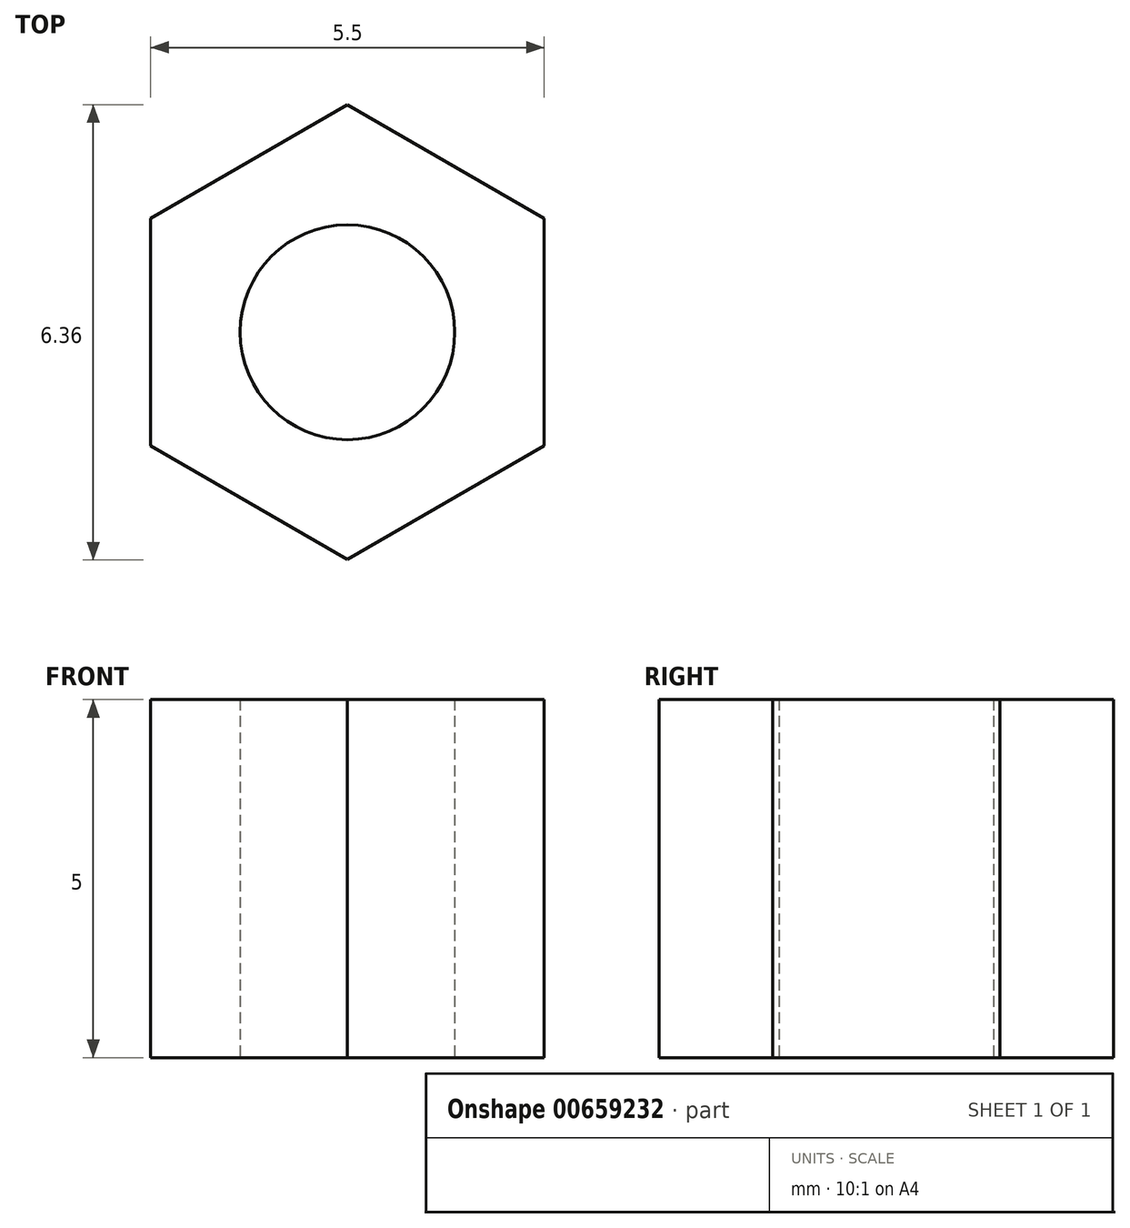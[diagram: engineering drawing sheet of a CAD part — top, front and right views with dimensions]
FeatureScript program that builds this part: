
annotation { "Feature Type Name" : "Feature", "Feature Type Description" : "" }
export const myFeature = defineFeature(function(context is Context, id is Id, definition is map)
    precondition{}
    {
        {
            var Q0;
            Q0=qCreatedBy(makeId("Top.planeOp"),FACE);
            var sketch = newSketch(context, id + "F0", { "sketchPlane" : qUnion([Q0])});
            skCircle(sketch, "E0.cCircle", {"center": v(0, 0) * mm, "radius": 2.75 * mm, "construction": true});
            skLineSegment(sketch, "E0.0", {"start": v(2.75, 1.59) * mm, "end": v(2.75, -1.59) * mm});
            skLineSegment(sketch, "E0.1", {"start": v(2.75, -1.59) * mm, "end": v(0, -3.18) * mm});
            skLineSegment(sketch, "E0.2", {"start": v(0, -3.18) * mm, "end": v(-2.75, -1.59) * mm});
            skLineSegment(sketch, "E0.3", {"start": v(-2.75, -1.59) * mm, "end": v(-2.75, 1.59) * mm});
            skLineSegment(sketch, "E0.4", {"start": v(-2.75, 1.59) * mm, "end": v(0, 3.18) * mm});
            skLineSegment(sketch, "E0.5", {"start": v(0, 3.18) * mm, "end": v(2.75, 1.59) * mm});
            skPoint(sketch, "E0.0.midPoint", {"position": v(2.75, 0) * mm});
            skCircle(sketch, "E1", {"center": v(0, 0) * mm, "radius": 1.5 * mm});
            skSolve(sketch);
        }
        {
            var Q0;
            Q0=makeQuery(id+"F0.imprint","IMPRINT",FACE,{"disambiguationData":[TD([[makeQuery(id+"F0.imprint","IMPRINT",EDGE,{"derivedFrom":sQuery(id+"F0.wireOp",EDGE,"E0.0")}),-1.0]])]});
            extrude(context, id + "F1", {"entities" : qUnion([Q0]), "depth" : 5 * mm, "offsetDistance" : 25 * mm});
        }
    });
